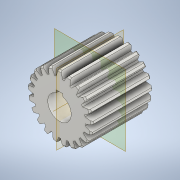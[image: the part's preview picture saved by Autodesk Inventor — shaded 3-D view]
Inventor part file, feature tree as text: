
AUTODESK INVENTOR PART (.ipt)
format: ipt  version: 2020 (Build 240168000, 168)  size: 444,416 bytes
history: native  units: mm (DEFAULTED — no unit token found)
features: plane x5, sketch x4, other x3, extrude x2, revolve x1, mirror x1
ambient origin geometry x8: Origin, YZ Plane, XZ Plane, XY Plane, X Axis, Y Axis, Z Axis, Center Point
bodies: Solid1 (feature_tree)
feature tree (16):
  extrude  "Extrusion1"  Depth=130.0mm TaperAngle=0.0deg
  plane  "Work Plane2"
  plane  "Work Plane8"
  plane  "Work Plane9"
  other  "正齿轮"
  extrude  "拉伸2"  Depth=10.0mm TaperAngle=0.0deg
  other  "工作轴1"
  plane  "工作平面11"
  revolve  "旋转1"  [1 undecoded]
  plane  "工作平面12"
  mirror  "镜像1"
  sketch  "Sketch1"  dims[d0=138.0mm d1=130.0mm d2=0.0mm]
  sketch  "Sketch2"  dims[d3=126.0mm d4=10.0mm d5=0.0mm]
  other  "Srf1"
  sketch  "草图3"  dims[d16=357.0mm d17=0.0mm d34=1.495997mm]
  sketch  "草图4"  dims[d39=0.0mm d41=0.0mm d43=357.0mm d46=357.0mm d47=0.0mm d48=0.0mm d49=50.0mm d50=14.0mm d51=9.0mm d52=3.5mm d53=10.0mm d54=0.0mm d55=3.0mm d56=3.0mm d57=3.0mm d58=3.0mm d59=90.0deg]
note: 1 required parameter value undecoded (feature->parameter linkage not recoverable at this tier; creation-order binding heuristic only, values carry confidence <= 0.55)
